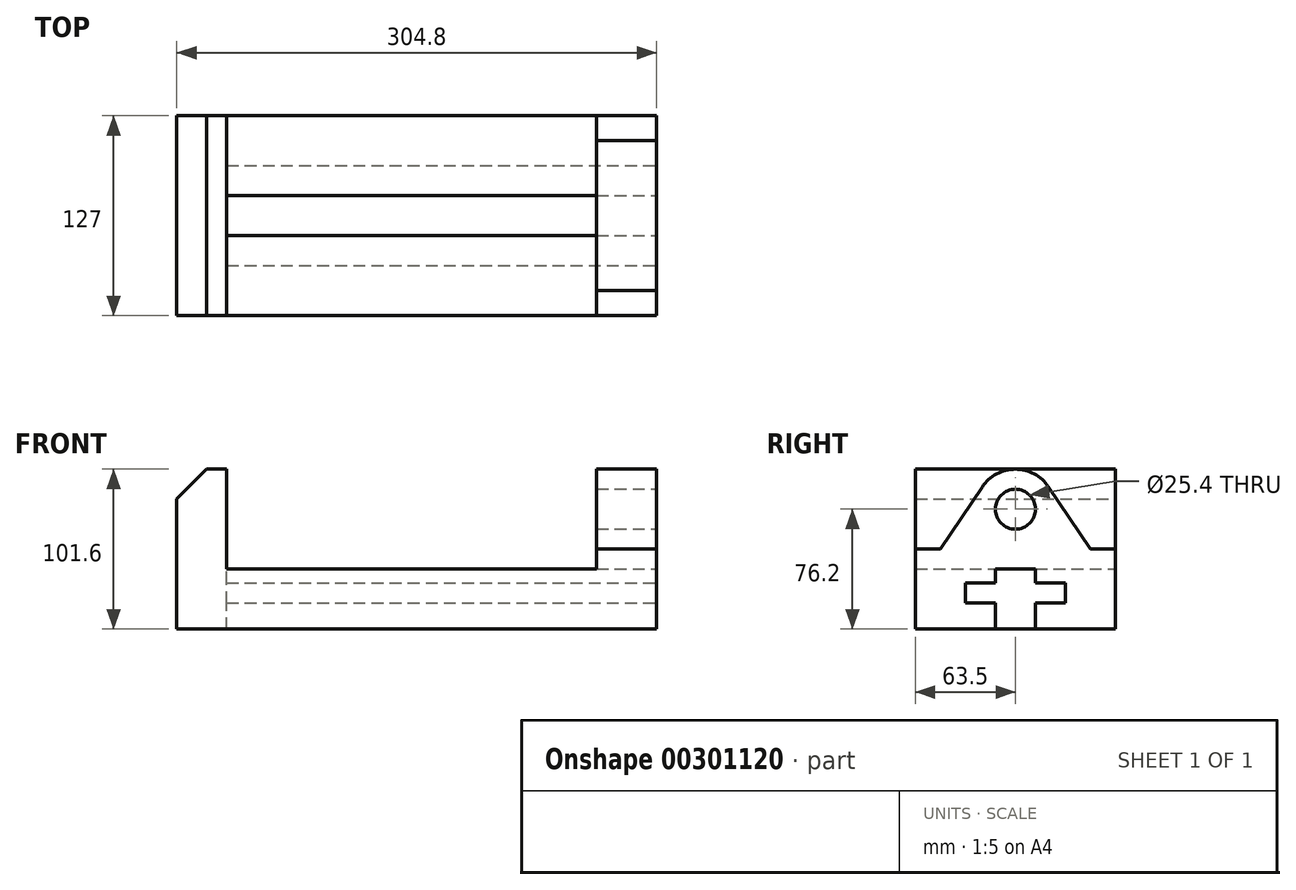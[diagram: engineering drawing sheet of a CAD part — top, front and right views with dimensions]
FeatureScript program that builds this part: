
annotation { "Feature Type Name" : "Feature", "Feature Type Description" : "" }
export const myFeature = defineFeature(function(context is Context, id is Id, definition is map)
    precondition{}
    {
        {
            var Q0;
            Q0=qCreatedBy(makeId("Front.planeOp"),FACE);
            var sketch = newSketch(context, id + "F0", { "sketchPlane" : qUnion([Q0])});
            skLineSegment(sketch, "E0", {"start": v(0, 0) * mm, "end": v(0, 82.55) * mm});
            skLineSegment(sketch, "E1", {"start": v(0, 82.55) * mm, "end": v(19.05, 101.6) * mm});
            skLineSegment(sketch, "E2", {"start": v(19.05, 101.6) * mm, "end": v(31.75, 101.6) * mm});
            skLineSegment(sketch, "E3", {"start": v(31.75, 101.6) * mm, "end": v(31.75, 38.1) * mm});
            skLineSegment(sketch, "E4", {"start": v(31.75, 38.1) * mm, "end": v(266.7, 38.1) * mm});
            skLineSegment(sketch, "E5", {"start": v(266.7, 38.1) * mm, "end": v(266.7, 50.8) * mm});
            skLineSegment(sketch, "E6", {"start": v(266.7, 50.8) * mm, "end": v(304.8, 50.8) * mm});
            skLineSegment(sketch, "E7", {"start": v(304.8, 50.8) * mm, "end": v(304.8, 0) * mm});
            skLineSegment(sketch, "E8", {"start": v(304.8, 0) * mm, "end": v(0, 0) * mm});
            skSolve(sketch);
        }
        {
            var Q0;
            Q0=makeQuery(id+"F0.imprint","IMPRINT",FACE,{"disambiguationData":[TD([[makeQuery(id+"F0.imprint","IMPRINT",EDGE,{"derivedFrom":sQuery(id+"F0.wireOp",EDGE,"E0")}),-1.0]])]});
            extrude(context, id + "F1", {"entities" : qUnion([Q0]), "depth" : 127 * mm});
        }
        {
            var Q0;
            Q0=makeQuery(id+"F1.opExtrude","SWEPT_FACE",FACE,{"disambiguationData":[OSD([sQuery(id+"F0.wireOp",EDGE,"E7")])]});
            var sketch = newSketch(context, id + "F2", { "sketchPlane" : qUnion([Q0])});
            skLineSegment(sketch, "E9", {"start": v(-127, 50.8) * mm, "end": v(-111.13, 50.8) * mm});
            skLineSegment(sketch, "E10", {"start": v(-111.13, 50.8) * mm, "end": v(-84.6, 90.35) * mm});
            skArc(sketch, "E11", {"start": v(-42.4, 90.35) * mm, "mid": v(-63.5, 101.6) * mm, "end": v(-84.6, 90.35) * mm});
            skLineSegment(sketch, "E12", {"start": v(-42.4, 90.35) * mm, "end": v(-15.87, 50.8) * mm});
            skLineSegment(sketch, "E13", {"start": v(-15.87, 50.8) * mm, "end": v(0, 50.8) * mm});
            skCircle(sketch, "E14", {"center": v(-63.5, 76.2) * mm, "radius": 12.7 * mm});
            skSolve(sketch);
        }
        {
            var Q0;
            {var subQ1=sQuery(id+"F2.wireOp",EDGE,"E10");Q0=makeQuery(id+"F2.imprint","IMPRINT",FACE,{"disambiguationData":[TD([[makeQuery(id+"F2.imprint","IMPRINT",EDGE,{"derivedFrom":subQ1}),-1.0]])]});}
            extrude(context, id + "F3", {"entities" : qUnion([Q0]), "operationType" : NewBodyOperationType.ADD, "oppositeDirection" : true, "depth" : 38.1 * mm});
        }
        {
            var Q0;
            {var subQ0=sQuery(id+"F0.wireOp",EDGE,"E7");Q0=makeQuery(id+"F3.boolean.opBoolean","MERGE",FACE,{"derivedFrom":[makeQuery(id+"F1.opExtrude","SWEPT_FACE",FACE,{"disambiguationData":[OSD([subQ0])]}),makeQuery(id+"F3.opExtrude","CAP_FACE",FACE,{"disambiguationData":[OSD([sQuery(id+"F0.wireOp",EDGE,"E6"),subQ0,sQuery(id+"F2.wireOp",EDGE,"E10"),sQuery(id+"F2.wireOp",EDGE,"E11"),sQuery(id+"F2.wireOp",EDGE,"E12"),sQuery(id+"F2.wireOp",EDGE,"E14")])],"isStart":true})]});}
            var sketch = newSketch(context, id + "F4", { "sketchPlane" : qUnion([Q0])});
            skLineSegment(sketch, "E15.bottom", {"start": v(-76.2, 0) * mm, "end": v(-50.8, 0) * mm});
            skLineSegment(sketch, "E15.left", {"start": v(-76.2, 0) * mm, "end": v(-76.2, 16.5) * mm});
            skLineSegment(sketch, "E15.right", {"start": v(-50.8, 0) * mm, "end": v(-50.8, 16.5) * mm});
            skLineSegment(sketch, "E16", {"start": v(-76.2, 16.5) * mm, "end": v(-95.25, 16.5) * mm});
            skLineSegment(sketch, "E17", {"start": v(-95.25, 16.5) * mm, "end": v(-95.25, 29.2) * mm});
            skLineSegment(sketch, "E18", {"start": v(-95.25, 29.2) * mm, "end": v(-76.2, 29.2) * mm});
            skLineSegment(sketch, "E19", {"start": v(-76.2, 29.2) * mm, "end": v(-76.2, 38.1) * mm});
            skLineSegment(sketch, "E20", {"start": v(-76.2, 38.1) * mm, "end": v(-50.8, 38.1) * mm});
            skLineSegment(sketch, "E21", {"start": v(-50.8, 38.1) * mm, "end": v(-50.8, 29.2) * mm});
            skLineSegment(sketch, "E22", {"start": v(-50.8, 29.2) * mm, "end": v(-31.75, 29.2) * mm});
            skLineSegment(sketch, "E23", {"start": v(-31.75, 29.2) * mm, "end": v(-31.75, 16.5) * mm});
            skLineSegment(sketch, "E24", {"start": v(-31.75, 16.5) * mm, "end": v(-50.8, 16.5) * mm});
            skPoint(sketch, "E25", {"position": v(-63.5, 38.1) * mm});
            skPoint(sketch, "E26", {"position": v(-63.5, 76.2) * mm});
            skSolve(sketch);
        }
        {
            var Q0;
            Q0 = qSketchRegion(id + "F4", true);
            extrude(context, id + "F5", {"entities" : qUnion([Q0]), "operationType" : NewBodyOperationType.REMOVE, "oppositeDirection" : true, "depth" : 273.05 * mm});
        }
    });
